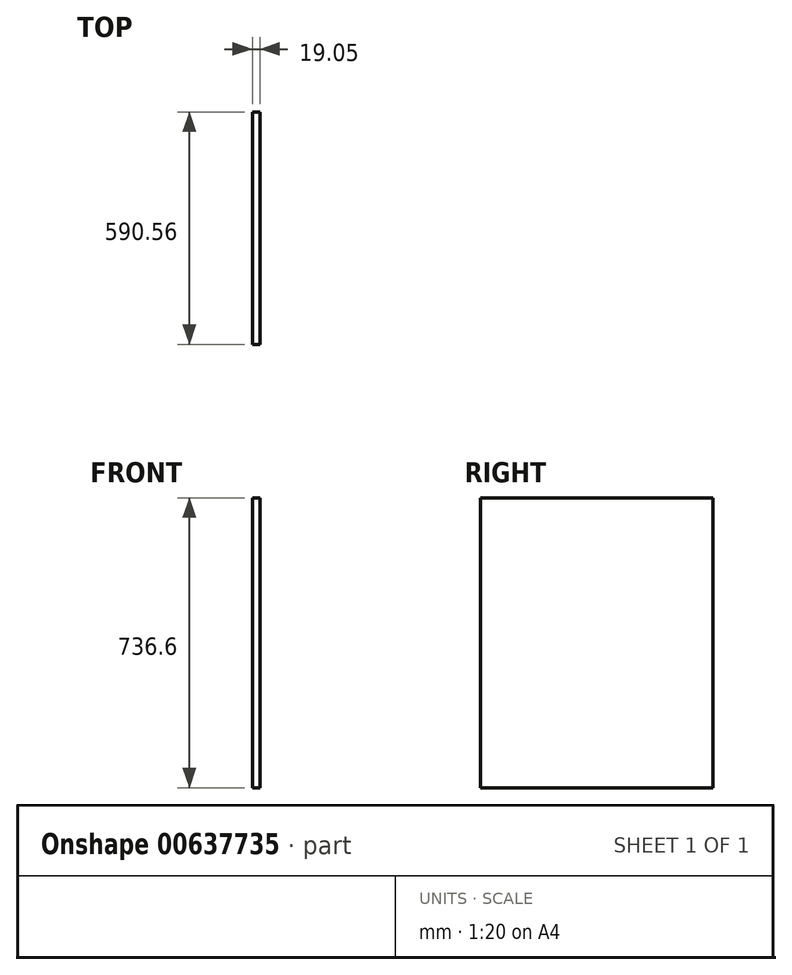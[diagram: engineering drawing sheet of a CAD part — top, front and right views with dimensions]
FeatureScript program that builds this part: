
annotation { "Feature Type Name" : "Feature", "Feature Type Description" : "" }
export const myFeature = defineFeature(function(context is Context, id is Id, definition is map)
    precondition{}
    {
        {
            var Q0;
            Q0=qCreatedBy(makeId("Right.planeOp"),FACE);
            var sketch = newSketch(context, id + "F0", { "sketchPlane" : qUnion([Q0])});
            skLineSegment(sketch, "E0.bottom", {"start": v(295.28, -368.3) * mm, "end": v(-295.28, -368.3) * mm});
            skLineSegment(sketch, "E0.top", {"start": v(295.28, 368.3) * mm, "end": v(-295.28, 368.3) * mm});
            skLineSegment(sketch, "E0.left", {"start": v(295.28, -368.3) * mm, "end": v(295.28, 368.3) * mm});
            skLineSegment(sketch, "E0.right", {"start": v(-295.28, -368.3) * mm, "end": v(-295.28, 368.3) * mm});
            skPoint(sketch, "E0.middle", {"position": v(0, 0) * mm});
            skSolve(sketch);
        }
        {
            var Q0;
            Q0 = qSketchRegion(id + "F0", true);
            extrude(context, id + "F1", {"entities" : qUnion([Q0]), "oppositeDirection" : true, "depth" : 19.05 * mm, "offsetDistance" : 25.4 * mm});
        }
        {
            var Q0;
            Q0 = qSketchRegion(id + "F0", true);
            extrude(context, id + "F2", {"entities" : qUnion([Q0]), "operationType" : NewBodyOperationType.ADD, "oppositeDirection" : true, "depth" : 19.05 * mm, "offsetDistance" : 25.4 * mm});
        }
    });
